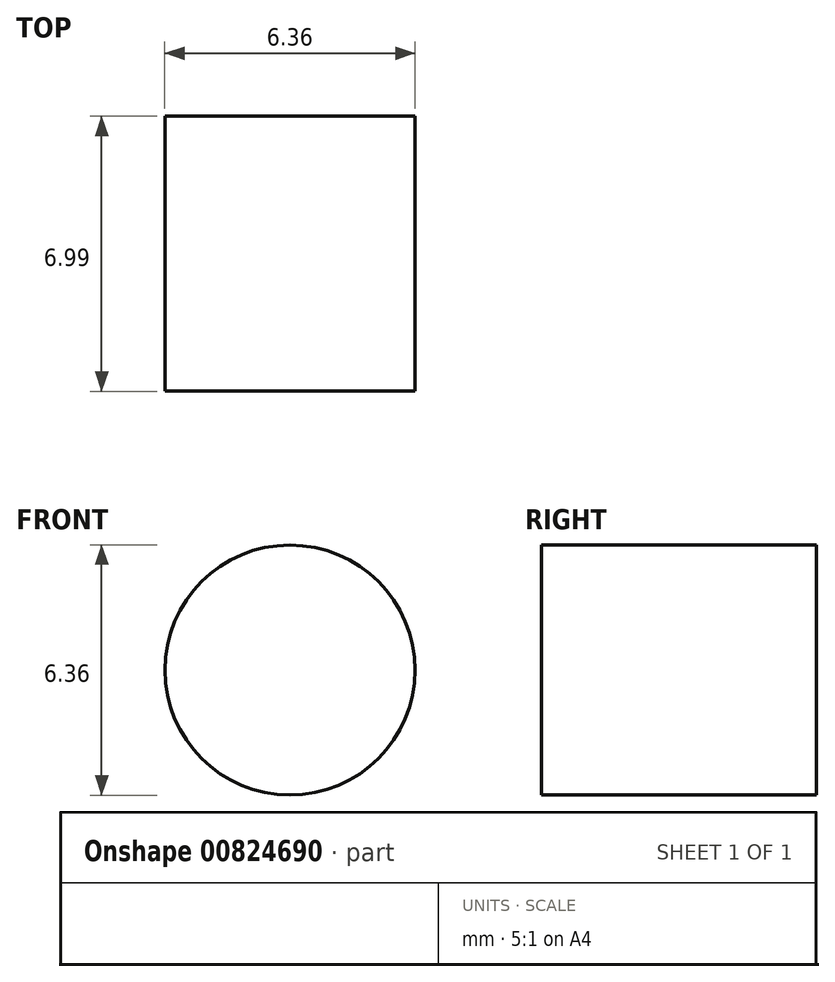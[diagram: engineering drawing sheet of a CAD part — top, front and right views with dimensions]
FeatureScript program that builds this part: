
annotation { "Feature Type Name" : "Feature", "Feature Type Description" : "" }
export const myFeature = defineFeature(function(context is Context, id is Id, definition is map)
    precondition{}
    {
        {
            var Q0;
            Q0=qCreatedBy(makeId("Front.planeOp"),FACE);
            var sketch = newSketch(context, id + "F0", { "sketchPlane" : qUnion([Q0])});
            skCircle(sketch, "E0", {"center": v(0, 0) * mm, "radius": 3.18 * mm});
            skSolve(sketch);
        }
        {
            var Q0;
            Q0 = qSketchRegion(id + "F0", true);
            extrude(context, id + "F1", {"entities" : qUnion([Q0]), "depth" : 7 * mm, "offsetDistance" : 25.4 * mm});
        }
    });
